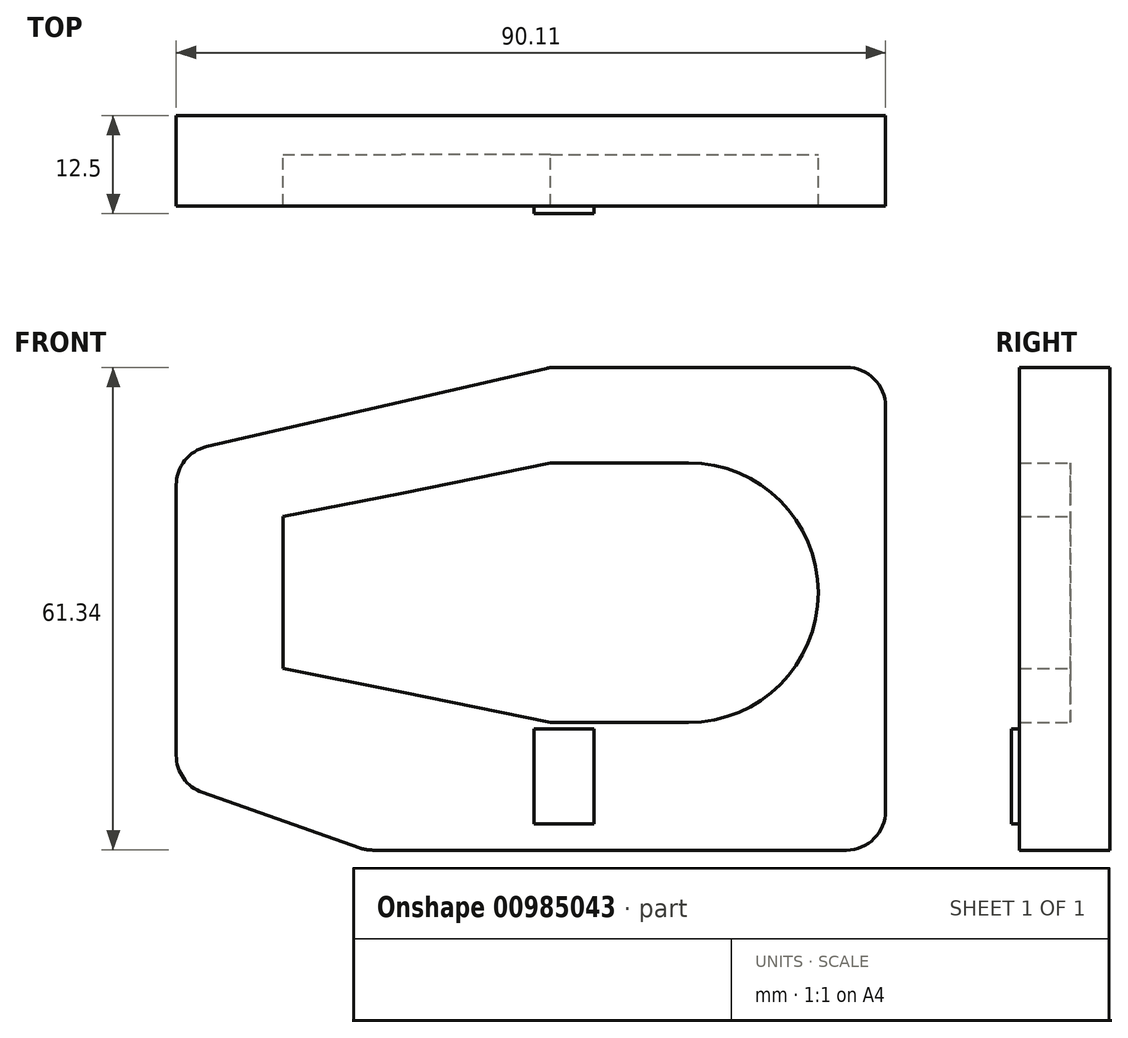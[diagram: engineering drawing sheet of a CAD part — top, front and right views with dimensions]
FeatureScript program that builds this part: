
annotation { "Feature Type Name" : "Feature", "Feature Type Description" : "" }
export const myFeature = defineFeature(function(context is Context, id is Id, definition is map)
    precondition{}
    {
        {
            var Q0;
            Q0=qCreatedBy(makeId("Front.planeOp"),FACE);
            var sketch = newSketch(context, id + "F0", { "sketchPlane" : qUnion([Q0])});
            skLineSegment(sketch, "E0.bottom", {"start": v(0, 16.5) * mm, "end": v(17.5, 16.5) * mm});
            skLineSegment(sketch, "E0.top", {"start": v(0, -16.5) * mm, "end": v(17.5, -16.5) * mm});
            skLineSegment(sketch, "E1.right", {"start": v(-34, 9.65) * mm, "end": v(-34, -9.65) * mm});
            skLineSegment(sketch, "E2", {"start": v(-34, 2.54) * mm, "end": v(-2.13, 2.54) * mm, "construction": true});
            skLineSegment(sketch, "E3", {"start": v(-34, -4.97) * mm, "end": v(5.5, -4.97) * mm, "construction": true});
            skArc(sketch, "E4", {"start": v(17.5, -16.5) * mm, "mid": v(34, 0) * mm, "end": v(17.5, 16.5) * mm});
            skLineSegment(sketch, "E5", {"start": v(0, 16.5) * mm, "end": v(-19, 12.62) * mm});
            skLineSegment(sketch, "E6", {"start": v(-19, 12.62) * mm, "end": v(-34, 9.65) * mm});
            skLineSegment(sketch, "E7", {"start": v(-34, -9.65) * mm, "end": v(-19, -12.63) * mm});
            skLineSegment(sketch, "E8", {"start": v(-19, -12.63) * mm, "end": v(0, -16.5) * mm});
            skLineSegment(sketch, "E9", {"start": v(31.07, 28.63) * mm, "end": v(0, 28.63) * mm});
            skLineSegment(sketch, "E10", {"start": v(0, 28.63) * mm, "end": v(-47.56, 17.65) * mm});
            skLineSegment(sketch, "E11", {"start": v(-47.56, 17.65) * mm, "end": v(-47.56, -24.21) * mm});
            skLineSegment(sketch, "E12", {"start": v(-47.56, -24.21) * mm, "end": v(-23.45, -32.71) * mm});
            skLineSegment(sketch, "E13", {"start": v(-23.45, -32.71) * mm, "end": v(42.55, -32.71) * mm});
            skLineSegment(sketch, "E14", {"start": v(42.55, -32.71) * mm, "end": v(42.55, 28.63) * mm});
            skLineSegment(sketch, "E15", {"start": v(42.55, 28.63) * mm, "end": v(31.07, 28.63) * mm});
            skSolve(sketch);
        }
        {
            var Q0;
            Q0=makeQuery(id+"F0.imprint","IMPRINT",FACE,{"disambiguationData":[TD([[makeQuery(id+"F0.imprint","IMPRINT",EDGE,{"derivedFrom":sQuery(id+"F0.wireOp",EDGE,"E0.bottom")}),1.0]])]});
            extrude(context, id + "F1", {"entities" : qUnion([Q0]), "depth" : 6.5 * mm, "offsetDistance" : 25 * mm});
        }
        {
            var Q0;
            Q0=makeQuery(id+"F0.imprint","IMPRINT",FACE,{"disambiguationData":[TD([[makeQuery(id+"F0.imprint","IMPRINT",EDGE,{"derivedFrom":sQuery(id+"F0.wireOp",EDGE,"E0.bottom")}),-1.0]])]});
            var Q1;
            Q1=makeQuery(id+"F0.imprint","IMPRINT",FACE,{"disambiguationData":[TD([[makeQuery(id+"F0.imprint","IMPRINT",EDGE,{"derivedFrom":sQuery(id+"F0.wireOp",EDGE,"E0.bottom")}),1.0]])]});
            extrude(context, id + "F2", {"entities" : qUnion([Q0, Q1]), "operationType" : NewBodyOperationType.ADD, "oppositeDirection" : true, "depth" : 5 * mm, "offsetDistance" : 25 * mm});
        }
        {
            var Q0;
            {var subQ0=sQuery(id+"F0.wireOp",EDGE,"E15");var subQ1=sQuery(id+"F0.wireOp",EDGE,"E14");Q0=makeQuery(id+"F2.boolean.opBoolean","MERGE",EDGE,{"derivedFrom":[makeQuery(id+"F1.opExtrude","SWEPT_EDGE",EDGE,{"disambiguationData":[OSD([subQ1,subQ0])]}),makeQuery(id+"F2.opExtrude","SWEPT_EDGE",EDGE,{"disambiguationData":[OSD([subQ1,subQ0])]})]});}
            var Q1;
            {var subQ0=sQuery(id+"F0.wireOp",EDGE,"E14");var subQ1=sQuery(id+"F0.wireOp",EDGE,"E13");Q1=makeQuery(id+"F2.boolean.opBoolean","MERGE",EDGE,{"derivedFrom":[makeQuery(id+"F1.opExtrude","SWEPT_EDGE",EDGE,{"disambiguationData":[OSD([subQ1,subQ0])]}),makeQuery(id+"F2.opExtrude","SWEPT_EDGE",EDGE,{"disambiguationData":[OSD([subQ1,subQ0])]})]});}
            var Q2;
            {var subQ0=sQuery(id+"F0.wireOp",EDGE,"E12");var subQ1=sQuery(id+"F0.wireOp",EDGE,"E11");Q2=makeQuery(id+"F2.boolean.opBoolean","MERGE",EDGE,{"derivedFrom":[makeQuery(id+"F1.opExtrude","SWEPT_EDGE",EDGE,{"disambiguationData":[OSD([subQ1,subQ0])]}),makeQuery(id+"F2.opExtrude","SWEPT_EDGE",EDGE,{"disambiguationData":[OSD([subQ1,subQ0])]})]});}
            var Q3;
            {var subQ0=sQuery(id+"F0.wireOp",EDGE,"E11");var subQ1=sQuery(id+"F0.wireOp",EDGE,"E10");Q3=makeQuery(id+"F2.boolean.opBoolean","MERGE",EDGE,{"derivedFrom":[makeQuery(id+"F1.opExtrude","SWEPT_EDGE",EDGE,{"disambiguationData":[OSD([subQ1,subQ0])]}),makeQuery(id+"F2.opExtrude","SWEPT_EDGE",EDGE,{"disambiguationData":[OSD([subQ1,subQ0])]})]});}
            var Q4;
            {var subQ0=sQuery(id+"F0.wireOp",EDGE,"E10");var subQ1=sQuery(id+"F0.wireOp",EDGE,"E9");Q4=makeQuery(id+"F2.boolean.opBoolean","MERGE",EDGE,{"derivedFrom":[makeQuery(id+"F1.opExtrude","SWEPT_EDGE",EDGE,{"disambiguationData":[OSD([subQ1,subQ0])]}),makeQuery(id+"F2.opExtrude","SWEPT_EDGE",EDGE,{"disambiguationData":[OSD([subQ1,subQ0])]})]});}
            var Q5;
            {var subQ0=sQuery(id+"F0.wireOp",EDGE,"E13");var subQ1=sQuery(id+"F0.wireOp",EDGE,"E12");Q5=makeQuery(id+"F2.boolean.opBoolean","MERGE",EDGE,{"derivedFrom":[makeQuery(id+"F1.opExtrude","SWEPT_EDGE",EDGE,{"disambiguationData":[OSD([subQ1,subQ0])]}),makeQuery(id+"F2.opExtrude","SWEPT_EDGE",EDGE,{"disambiguationData":[OSD([subQ1,subQ0])]})]});}
            fillet(context, id + "F3", {"entities" : qUnion([Q0, Q1, Q2, Q3, Q4, Q5]), "radius" : 5 * mm, "tangentPropagation" : true, "allowEdgeOverflow" : false});
        }
        {
            var Q0;
            Q0=makeQuery(id+"F1.opExtrude","CAP_FACE",FACE,{"disambiguationData":[OSD([sQuery(id+"F0.wireOp",EDGE,"E0.bottom"),sQuery(id+"F0.wireOp",EDGE,"E0.top"),sQuery(id+"F0.wireOp",EDGE,"E1.right"),sQuery(id+"F0.wireOp",EDGE,"E4"),sQuery(id+"F0.wireOp",EDGE,"E5"),sQuery(id+"F0.wireOp",EDGE,"E6"),sQuery(id+"F0.wireOp",EDGE,"E7"),sQuery(id+"F0.wireOp",EDGE,"E8"),sQuery(id+"F0.wireOp",EDGE,"E9"),sQuery(id+"F0.wireOp",EDGE,"E10"),sQuery(id+"F0.wireOp",EDGE,"E11"),sQuery(id+"F0.wireOp",EDGE,"E12"),sQuery(id+"F0.wireOp",EDGE,"E13"),sQuery(id+"F0.wireOp",EDGE,"E14"),sQuery(id+"F0.wireOp",EDGE,"E15")])],"isStart":false});
            var sketch = newSketch(context, id + "F4", { "sketchPlane" : qUnion([Q0])});
            skLineSegment(sketch, "E16.bottom", {"start": v(-2.13, -17.33) * mm, "end": v(5.5, -17.33) * mm});
            skLineSegment(sketch, "E16.top", {"start": v(-2.13, -29.37) * mm, "end": v(5.5, -29.37) * mm});
            skLineSegment(sketch, "E16.left", {"start": v(5.5, -17.33) * mm, "end": v(5.5, -29.37) * mm});
            skLineSegment(sketch, "E16.right", {"start": v(-2.13, -17.33) * mm, "end": v(-2.13, -29.37) * mm});
            skSolve(sketch);
        }
        {
            var Q0;
            Q0=makeQuery(id+"F4.imprint","IMPRINT",FACE,{"disambiguationData":[TD([[makeQuery(id+"F4.imprint","IMPRINT",EDGE,{"derivedFrom":sQuery(id+"F4.wireOp",EDGE,"E16.bottom")}),-1.0]])]});
            extrude(context, id + "F5", {"entities" : qUnion([Q0]), "operationType" : NewBodyOperationType.ADD, "depth" : 1 * mm, "offsetDistance" : 25 * mm});
        }
    });
